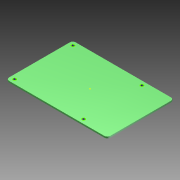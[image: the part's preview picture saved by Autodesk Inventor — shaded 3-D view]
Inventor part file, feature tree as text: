
AUTODESK INVENTOR PART (.ipt)
format: ipt  version: 2015 (Build 190159000, 159)  size: 95,744 bytes
history: native  units: in
note: dims shown in document units (in); Inventor stores cm internally (conversion verified against a paired STEP export)
features: other x2, sketch x1, imported_body x1
ambient origin geometry x8: Origin, YZ Plane, XZ Plane, XY Plane, X Axis, Y Axis, Z Axis, Center Point
bodies: Body1 (feature_tree)
feature tree (4):
  other  "Estrusione-Estrusione1"
  other  "Mainboard2.ipt1"
  sketch  "Sketch1"
  imported_body  "Base1"
